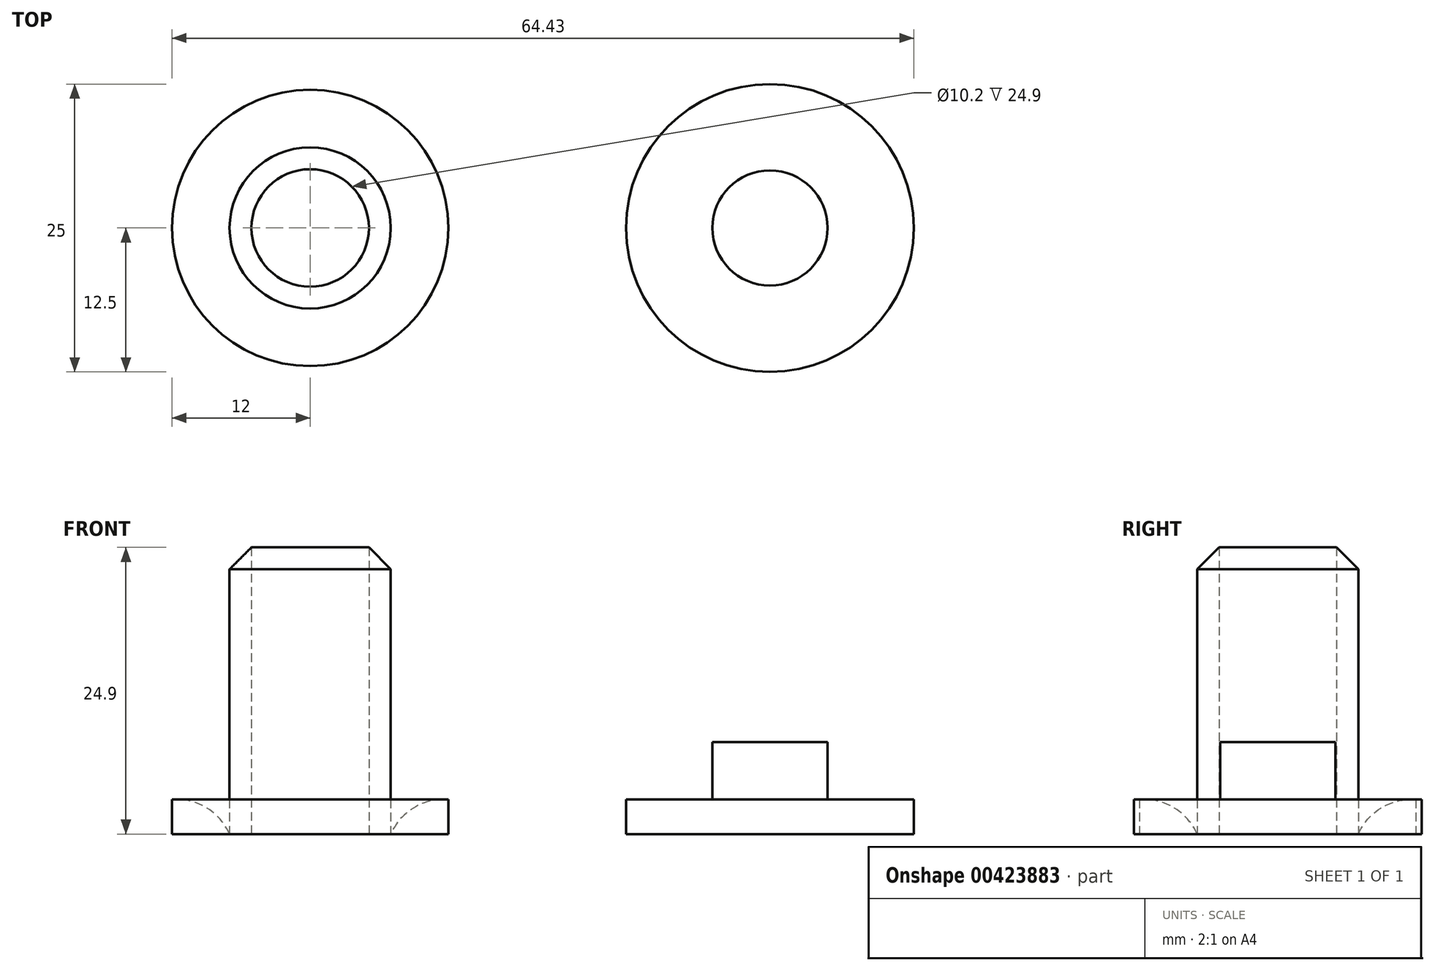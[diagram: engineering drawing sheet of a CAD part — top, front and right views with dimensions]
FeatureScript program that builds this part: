
annotation { "Feature Type Name" : "Feature", "Feature Type Description" : "" }
export const myFeature = defineFeature(function(context is Context, id is Id, definition is map)
    precondition{}
    {
        {
            var Q0;
            Q0=qCreatedBy(makeId("Top.planeOp"),FACE);
            var sketch = newSketch(context, id + "F0", { "sketchPlane" : qUnion([Q0])});
            skCircle(sketch, "E0", {"center": v(0, 0) * mm, "radius": 7 * mm});
            skCircle(sketch, "E1", {"center": v(0, 0) * mm, "radius": 5.1 * mm});
            skCircle(sketch, "E2", {"center": v(0, 0) * mm, "radius": 12 * mm});
            skSolve(sketch);
        }
        {
            var Q0;
            Q0=makeQuery(id+"F0.imprint","IMPRINT",FACE,{"disambiguationData":[TD([[makeQuery(id+"F0.imprint","IMPRINT",EDGE,{"derivedFrom":sQuery(id+"F0.wireOp",EDGE,"E0")}),1.0]])]});
            extrude(context, id + "F1", {"entities" : qUnion([Q0]), "depth" : 25 * mm});
        }
        {
            var Q0;
            Q0=makeQuery(id+"F0.imprint","IMPRINT",FACE,{"disambiguationData":[TD([[makeQuery(id+"F0.imprint","IMPRINT",EDGE,{"derivedFrom":sQuery(id+"F0.wireOp",EDGE,"E0")}),-1.0]])]});
            extrude(context, id + "F2", {"entities" : qUnion([Q0]), "depth" : 3 * mm});
        }
        {
            var Q0;
            Q0=makeQuery(id+"F2.opExtrude","CAP_EDGE",EDGE,{"disambiguationData":[OSD([sQuery(id+"F0.wireOp",EDGE,"E0")])],"isStart":false});
            fillet(context, id + "F3", {"entities" : qUnion([Q0]), "radius" : 5 * mm, "tangentPropagation" : true, "allowEdgeOverflow" : false});
        }
        {
            var Q0;
            Q0=makeQuery(id+"F1.opExtrude","CAP_EDGE",EDGE,{"disambiguationData":[OSD([sQuery(id+"F0.wireOp",EDGE,"E0")])],"isStart":false});
            chamfer(context, id + "F4", {"entities" : qUnion([Q0]), "width" : 2 * mm, "tangentPropagation" : true});
        }
        {
            var Q0;
            Q0=qCreatedBy(makeId("Top.planeOp"),FACE);
            var sketch = newSketch(context, id + "F5", { "sketchPlane" : qUnion([Q0])});
            skCircle(sketch, "E3", {"center": v(39.93, 0) * mm, "radius": 12.5 * mm});
            skSolve(sketch);
        }
        {
            var Q0;
            Q0 = qSketchRegion(id + "F5", true);
            extrude(context, id + "F6", {"entities" : qUnion([Q0]), "depth" : 3 * mm});
        }
        {
            var Q0;
            Q0=makeQuery(id+"F6.opExtrude","CAP_FACE",FACE,{"disambiguationData":[OSD([sQuery(id+"F5.wireOp",EDGE,"E3")])],"isStart":false});
            var sketch = newSketch(context, id + "F7", { "sketchPlane" : qUnion([Q0])});
            skCircle(sketch, "E4", {"center": v(39.93, 0) * mm, "radius": 5 * mm});
            skSolve(sketch);
        }
        {
            var Q0;
            Q0 = qSketchRegion(id + "F7", true);
            extrude(context, id + "F8", {"entities" : qUnion([Q0]), "operationType" : NewBodyOperationType.ADD, "depth" : 5 * mm});
        }
    });
